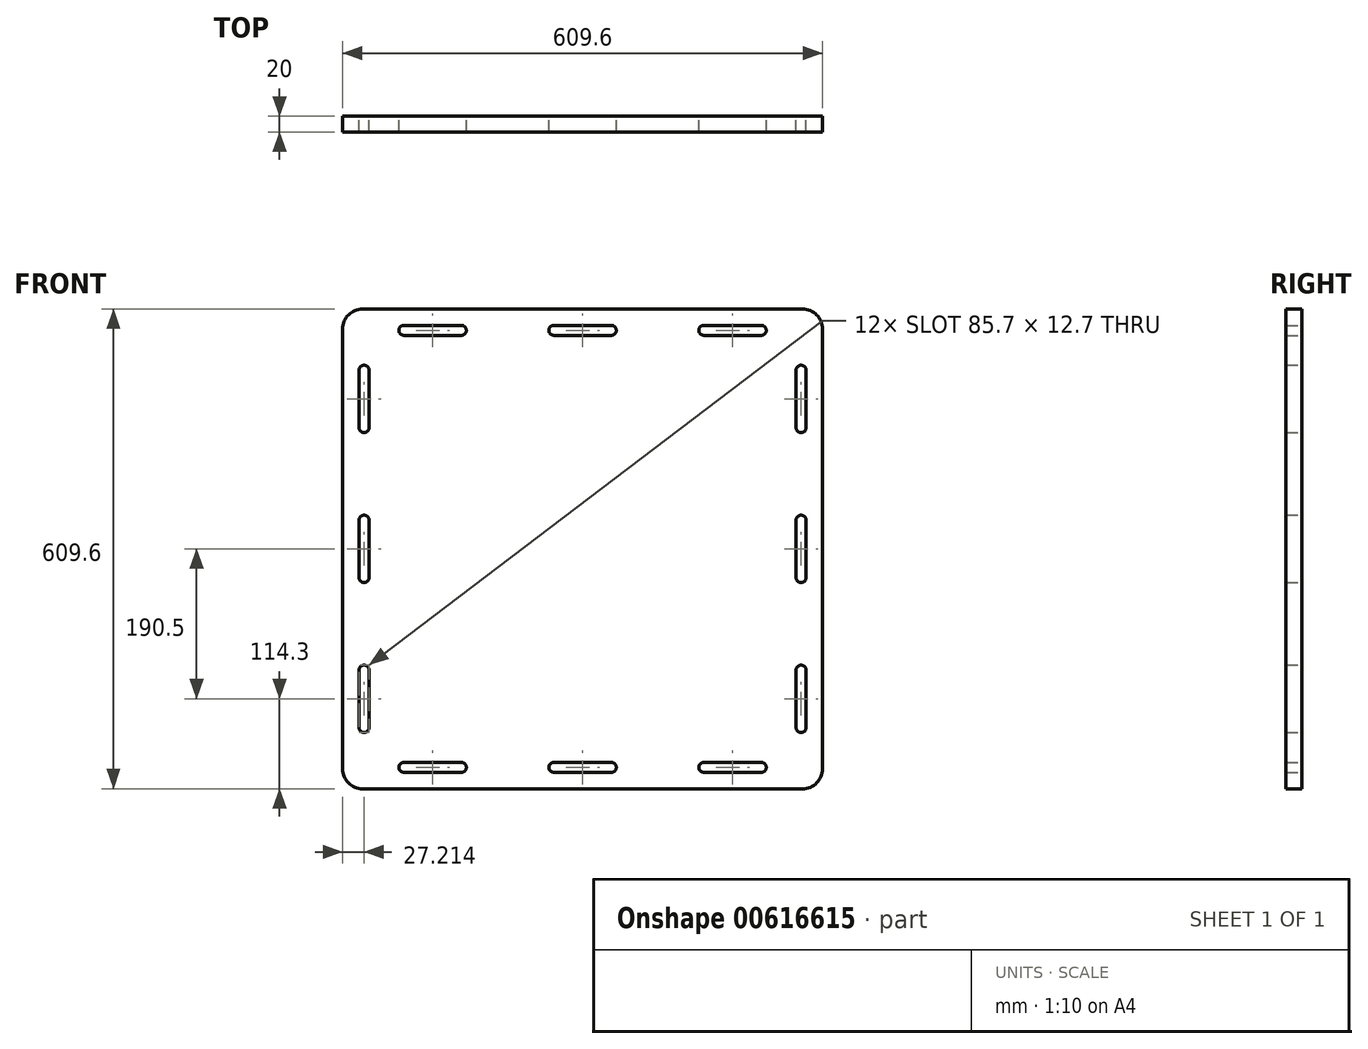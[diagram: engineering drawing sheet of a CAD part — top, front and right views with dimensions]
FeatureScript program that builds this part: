
annotation { "Feature Type Name" : "Feature", "Feature Type Description" : "" }
export const myFeature = defineFeature(function(context is Context, id is Id, definition is map)
    precondition{}
    {
        {
            var Q0;
            Q0=qCreatedBy(makeId("Front.planeOp"),FACE);
            var sketch = newSketch(context, id + "F0", { "sketchPlane" : qUnion([Q0])});
            skArc(sketch, "E0", {"start": v(279.4, -304.8) * mm, "mid": v(297.36, -297.36) * mm, "end": v(304.8, -279.4) * mm});
            skArc(sketch, "E1", {"start": v(-304.8, -279.4) * mm, "mid": v(-297.36, -297.36) * mm, "end": v(-279.4, -304.8) * mm});
            skArc(sketch, "E2", {"start": v(-279.4, 304.8) * mm, "mid": v(-297.36, 297.36) * mm, "end": v(-304.8, 279.4) * mm});
            skArc(sketch, "E3", {"start": v(304.8, 279.4) * mm, "mid": v(297.36, 297.36) * mm, "end": v(279.4, 304.8) * mm});
            skLineSegment(sketch, "E4", {"start": v(271.24, 227) * mm, "end": v(271.24, 154) * mm});
            skArc(sketch, "E5", {"start": v(271.24, 154) * mm, "mid": v(277.59, 147.65) * mm, "end": v(283.94, 154) * mm});
            skLineSegment(sketch, "E6", {"start": v(283.94, 154) * mm, "end": v(283.94, 227) * mm});
            skArc(sketch, "E7", {"start": v(283.94, 227) * mm, "mid": v(277.59, 233.35) * mm, "end": v(271.24, 227) * mm});
            skLineSegment(sketch, "E8", {"start": v(271.24, -154) * mm, "end": v(271.24, -227) * mm});
            skArc(sketch, "E9", {"start": v(271.24, -227) * mm, "mid": v(277.59, -233.35) * mm, "end": v(283.94, -227) * mm});
            skLineSegment(sketch, "E10", {"start": v(283.94, -227) * mm, "end": v(283.94, -154) * mm});
            skArc(sketch, "E11", {"start": v(283.94, -154) * mm, "mid": v(277.59, -147.65) * mm, "end": v(271.24, -154) * mm});
            skLineSegment(sketch, "E12", {"start": v(271.24, 36.5) * mm, "end": v(271.24, -36.5) * mm});
            skArc(sketch, "E13", {"start": v(271.24, -36.5) * mm, "mid": v(277.59, -42.85) * mm, "end": v(283.94, -36.5) * mm});
            skLineSegment(sketch, "E14", {"start": v(283.94, -36.5) * mm, "end": v(283.94, 36.5) * mm});
            skArc(sketch, "E15", {"start": v(283.94, 36.5) * mm, "mid": v(277.59, 42.85) * mm, "end": v(271.24, 36.5) * mm});
            skLineSegment(sketch, "E16", {"start": v(-227, 271.24) * mm, "end": v(-154, 271.24) * mm});
            skArc(sketch, "E17", {"start": v(-154, 271.24) * mm, "mid": v(-147.65, 277.59) * mm, "end": v(-154, 283.94) * mm});
            skLineSegment(sketch, "E18", {"start": v(-154, 283.94) * mm, "end": v(-227, 283.94) * mm});
            skArc(sketch, "E19", {"start": v(-227, 283.94) * mm, "mid": v(-233.35, 277.59) * mm, "end": v(-227, 271.24) * mm});
            skLineSegment(sketch, "E20", {"start": v(154, 271.24) * mm, "end": v(227, 271.24) * mm});
            skArc(sketch, "E21", {"start": v(227, 271.24) * mm, "mid": v(233.35, 277.59) * mm, "end": v(227, 283.94) * mm});
            skLineSegment(sketch, "E22", {"start": v(227, 283.94) * mm, "end": v(154, 283.94) * mm});
            skArc(sketch, "E23", {"start": v(154, 283.94) * mm, "mid": v(147.65, 277.59) * mm, "end": v(154, 271.24) * mm});
            skLineSegment(sketch, "E24", {"start": v(-36.5, 271.24) * mm, "end": v(36.5, 271.24) * mm});
            skArc(sketch, "E25", {"start": v(36.5, 271.24) * mm, "mid": v(42.85, 277.59) * mm, "end": v(36.5, 283.94) * mm});
            skLineSegment(sketch, "E26", {"start": v(36.5, 283.94) * mm, "end": v(-36.5, 283.94) * mm});
            skArc(sketch, "E27", {"start": v(-36.5, 283.94) * mm, "mid": v(-42.85, 277.59) * mm, "end": v(-36.5, 271.24) * mm});
            skLineSegment(sketch, "E28", {"start": v(-271.24, -227) * mm, "end": v(-271.24, -154) * mm});
            skArc(sketch, "E29", {"start": v(-271.24, -154) * mm, "mid": v(-277.59, -147.65) * mm, "end": v(-283.94, -154) * mm});
            skLineSegment(sketch, "E30", {"start": v(-283.94, -154) * mm, "end": v(-283.94, -227) * mm});
            skArc(sketch, "E31", {"start": v(-283.94, -227) * mm, "mid": v(-277.59, -233.35) * mm, "end": v(-271.24, -227) * mm});
            skLineSegment(sketch, "E32", {"start": v(-271.24, 154) * mm, "end": v(-271.24, 227) * mm});
            skArc(sketch, "E33", {"start": v(-271.24, 227) * mm, "mid": v(-277.59, 233.35) * mm, "end": v(-283.94, 227) * mm});
            skLineSegment(sketch, "E34", {"start": v(-283.94, 227) * mm, "end": v(-283.94, 154) * mm});
            skArc(sketch, "E35", {"start": v(-283.94, 154) * mm, "mid": v(-277.59, 147.65) * mm, "end": v(-271.24, 154) * mm});
            skLineSegment(sketch, "E36", {"start": v(-271.24, -36.5) * mm, "end": v(-271.24, 36.5) * mm});
            skArc(sketch, "E37", {"start": v(-271.24, 36.5) * mm, "mid": v(-277.59, 42.85) * mm, "end": v(-283.94, 36.5) * mm});
            skLineSegment(sketch, "E38", {"start": v(-283.94, 36.5) * mm, "end": v(-283.94, -36.5) * mm});
            skArc(sketch, "E39", {"start": v(-283.94, -36.5) * mm, "mid": v(-277.59, -42.85) * mm, "end": v(-271.24, -36.5) * mm});
            skLineSegment(sketch, "E40", {"start": v(227, -271.24) * mm, "end": v(154, -271.24) * mm});
            skArc(sketch, "E41", {"start": v(154, -271.24) * mm, "mid": v(147.65, -277.59) * mm, "end": v(154, -283.94) * mm});
            skLineSegment(sketch, "E42", {"start": v(154, -283.94) * mm, "end": v(227, -283.94) * mm});
            skArc(sketch, "E43", {"start": v(227, -283.94) * mm, "mid": v(233.35, -277.59) * mm, "end": v(227, -271.24) * mm});
            skLineSegment(sketch, "E44", {"start": v(-154, -271.24) * mm, "end": v(-227, -271.24) * mm});
            skArc(sketch, "E45", {"start": v(-227, -271.24) * mm, "mid": v(-233.35, -277.59) * mm, "end": v(-227, -283.94) * mm});
            skLineSegment(sketch, "E46", {"start": v(-227, -283.94) * mm, "end": v(-154, -283.94) * mm});
            skArc(sketch, "E47", {"start": v(-154, -283.94) * mm, "mid": v(-147.65, -277.59) * mm, "end": v(-154, -271.24) * mm});
            skLineSegment(sketch, "E48", {"start": v(36.5, -271.24) * mm, "end": v(-36.5, -271.24) * mm});
            skArc(sketch, "E49", {"start": v(-36.5, -271.24) * mm, "mid": v(-42.85, -277.59) * mm, "end": v(-36.5, -283.94) * mm});
            skLineSegment(sketch, "E50", {"start": v(-36.5, -283.94) * mm, "end": v(36.5, -283.94) * mm});
            skArc(sketch, "E51", {"start": v(36.5, -283.94) * mm, "mid": v(42.85, -277.59) * mm, "end": v(36.5, -271.24) * mm});
            skLineSegment(sketch, "E52", {"start": v(279.4, 304.8) * mm, "end": v(-279.4, 304.8) * mm});
            skLineSegment(sketch, "E53", {"start": v(304.8, -279.4) * mm, "end": v(304.8, 279.4) * mm});
            skLineSegment(sketch, "E54", {"start": v(-279.4, -304.8) * mm, "end": v(279.4, -304.8) * mm});
            skLineSegment(sketch, "E55", {"start": v(-304.8, 279.4) * mm, "end": v(-304.8, -279.4) * mm});
            skSolve(sketch);
        }
        {
            var Q0;
            Q0=makeQuery(id+"F0.imprint","IMPRINT",FACE,{"disambiguationData":[TD([[makeQuery(id+"F0.imprint","IMPRINT",EDGE,{"derivedFrom":sQuery(id+"F0.wireOp",EDGE,"E0")}),1.0]])]});
            extrude(context, id + "F1", {"entities" : qUnion([Q0]), "depth" : 20 * mm, "offsetDistance" : 25 * mm});
        }
    });
